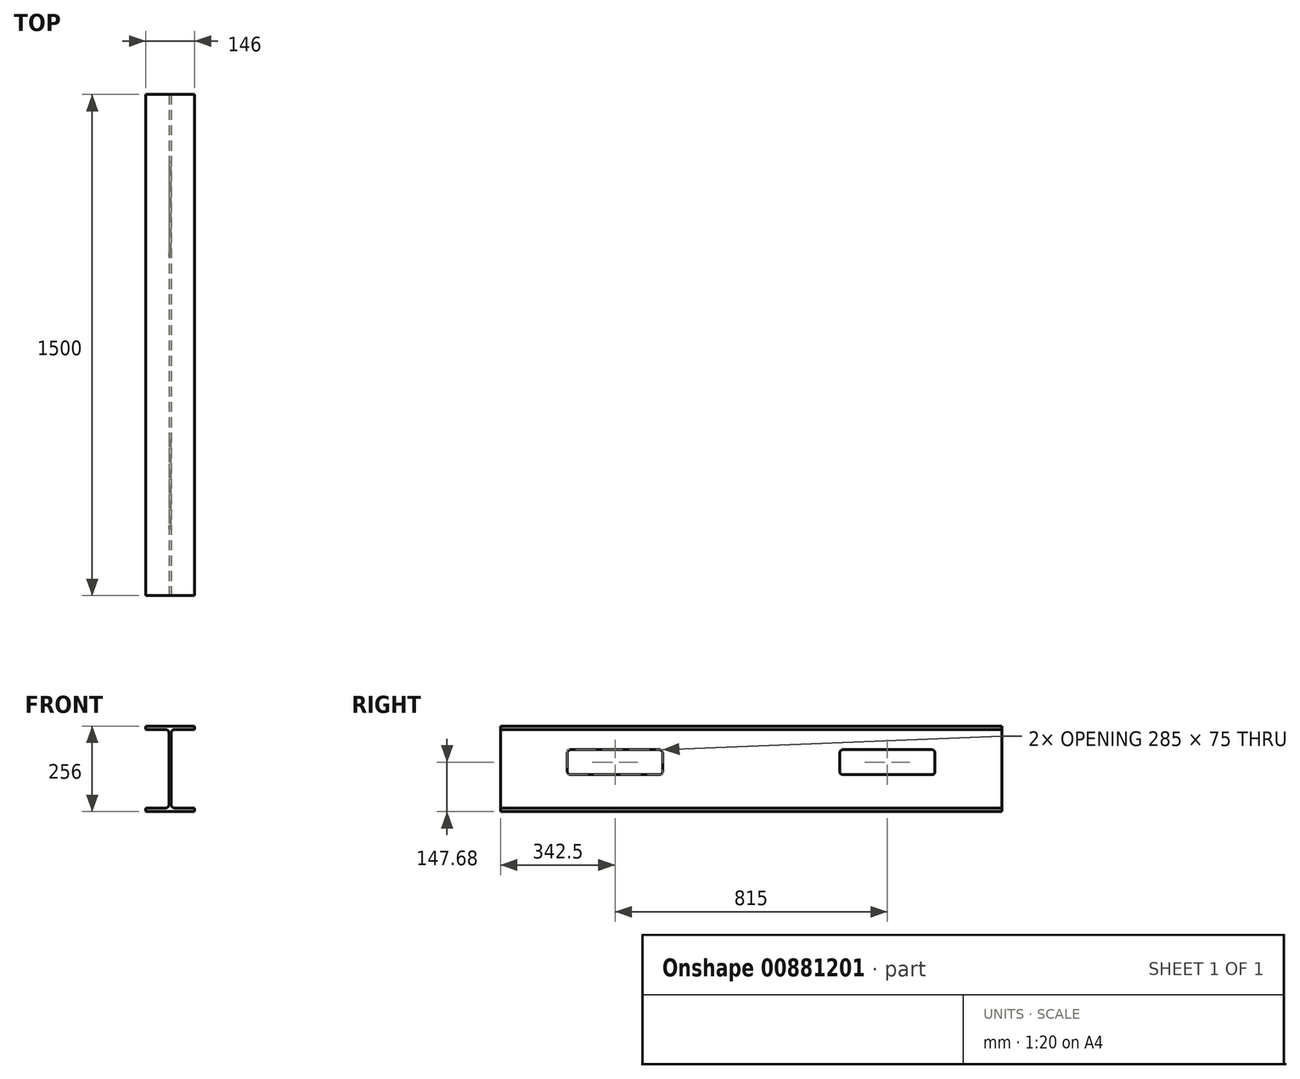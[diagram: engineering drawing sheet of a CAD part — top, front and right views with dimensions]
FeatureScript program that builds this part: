
annotation { "Feature Type Name" : "Feature", "Feature Type Description" : "" }
export const myFeature = defineFeature(function(context is Context, id is Id, definition is map)
    precondition{}
    {
        {
            var Q0;
            Q0=qCreatedBy(makeId("Front.planeOp"),FACE);
            var sketch = newSketch(context, id + "F0", { "sketchPlane" : qUnion([Q0])});
            skLineSegment(sketch, "E0", {"start": v(0, 147.9) * mm, "end": v(0, -157.79) * mm, "construction": true});
            skLineSegment(sketch, "E1", {"start": v(0, 108.32) * mm, "end": v(73, 108.32) * mm});
            skLineSegment(sketch, "E2", {"start": v(73, 108.32) * mm, "end": v(73, 97.42) * mm});
            skLineSegment(sketch, "E3", {"start": v(73, 97.42) * mm, "end": v(13.2, 97.42) * mm});
            skLineSegment(sketch, "E4", {"start": v(13.2, -136.78) * mm, "end": v(73, -136.78) * mm});
            skLineSegment(sketch, "E5", {"start": v(73, -136.78) * mm, "end": v(73, -147.68) * mm});
            skLineSegment(sketch, "E6", {"start": v(73, -147.68) * mm, "end": v(0, -147.68) * mm});
            skLineSegment(sketch, "E7", {"start": v(3.2, 87.42) * mm, "end": v(3.2, -126.78) * mm});
            skLineSegment(sketch, "E8.MirrorCS", {"start": v(0, 108.32) * mm, "end": v(-73, 108.32) * mm});
            skLineSegment(sketch, "E9.MirrorCS", {"start": v(-73, 108.32) * mm, "end": v(-73, 97.42) * mm});
            skLineSegment(sketch, "E10.MirrorCS", {"start": v(-73, 97.42) * mm, "end": v(-13.2, 97.42) * mm});
            skLineSegment(sketch, "E11.MirrorCS", {"start": v(-3.2, 87.42) * mm, "end": v(-3.2, -126.78) * mm});
            skLineSegment(sketch, "E12.MirrorCS", {"start": v(-13.2, -136.78) * mm, "end": v(-73, -136.78) * mm});
            skLineSegment(sketch, "E13.MirrorCS", {"start": v(-73, -136.78) * mm, "end": v(-73, -147.68) * mm});
            skLineSegment(sketch, "E14.MirrorCS", {"start": v(-73, -147.68) * mm, "end": v(0, -147.68) * mm});
            skPoint(sketch, "E15.visualSharp", {"position": v(3.2, 97.42) * mm});
            skArc(sketch, "E15.filletArc", {"start": v(13.2, 97.42) * mm, "mid": v(6.13, 94.5) * mm, "end": v(3.2, 87.42) * mm});
            skPoint(sketch, "E16.visualSharp", {"position": v(-3.2, 97.42) * mm});
            skArc(sketch, "E16.filletArc", {"start": v(-3.2, 87.42) * mm, "mid": v(-6.13, 94.5) * mm, "end": v(-13.2, 97.42) * mm});
            skPoint(sketch, "E17.visualSharp", {"position": v(-3.2, -136.78) * mm});
            skArc(sketch, "E17.filletArc", {"start": v(-13.2, -136.78) * mm, "mid": v(-6.13, -133.85) * mm, "end": v(-3.2, -126.78) * mm});
            skPoint(sketch, "E18.visualSharp", {"position": v(3.2, -136.78) * mm});
            skArc(sketch, "E18.filletArc", {"start": v(3.2, -126.78) * mm, "mid": v(6.13, -133.85) * mm, "end": v(13.2, -136.78) * mm});
            skSolve(sketch);
        }
        {
            var Q0;
            Q0=makeQuery(id+"F0.imprint","IMPRINT",FACE,{"disambiguationData":[TD([[makeQuery(id+"F0.imprint","IMPRINT",EDGE,{"derivedFrom":sQuery(id+"F0.wireOp",EDGE,"E1")}),-1.0]])]});
            extrude(context, id + "F1", {"entities" : qUnion([Q0]), "oppositeDirection" : true, "depth" : 1500 * mm, "offsetDistance" : 25 * mm});
        }
        {
            var Q0;
            Q0=makeQuery(id+"F1.opExtrude","SWEPT_FACE",FACE,{"disambiguationData":[OSD([sQuery(id+"F0.wireOp",EDGE,"E7")])]});
            var sketch = newSketch(context, id + "F2", { "sketchPlane" : qUnion([Q0])});
            skLineSegment(sketch, "E19.bottom", {"start": v(210, 37.5) * mm, "end": v(475, 37.5) * mm});
            skLineSegment(sketch, "E19.top", {"start": v(210, -37.5) * mm, "end": v(475, -37.5) * mm});
            skLineSegment(sketch, "E19.left", {"start": v(200, 27.5) * mm, "end": v(200, -27.5) * mm});
            skLineSegment(sketch, "E19.right", {"start": v(485, 27.5) * mm, "end": v(485, -27.5) * mm});
            skLineSegment(sketch, "E20", {"start": v(0, 0) * mm, "end": v(1500, 0) * mm, "construction": true});
            skPoint(sketch, "E21.visualSharp", {"position": v(200, 37.5) * mm});
            skArc(sketch, "E21.filletArc", {"start": v(210, 37.5) * mm, "mid": v(202.93, 34.57) * mm, "end": v(200, 27.5) * mm});
            skPoint(sketch, "E22.visualSharp", {"position": v(485, 37.5) * mm});
            skArc(sketch, "E22.filletArc", {"start": v(485, 27.5) * mm, "mid": v(482.07, 34.57) * mm, "end": v(475, 37.5) * mm});
            skPoint(sketch, "E23.visualSharp", {"position": v(485, -37.5) * mm});
            skArc(sketch, "E23.filletArc", {"start": v(475, -37.5) * mm, "mid": v(482.07, -34.57) * mm, "end": v(485, -27.5) * mm});
            skPoint(sketch, "E24.visualSharp", {"position": v(200, -37.5) * mm});
            skArc(sketch, "E24.filletArc", {"start": v(200, -27.5) * mm, "mid": v(202.93, -34.57) * mm, "end": v(210, -37.5) * mm});
            skLineSegment(sketch, "E25.bottom", {"start": v(1025, 37.5) * mm, "end": v(1290, 37.5) * mm});
            skLineSegment(sketch, "E25.top", {"start": v(1025, -37.5) * mm, "end": v(1290, -37.5) * mm});
            skLineSegment(sketch, "E25.left", {"start": v(1015, 27.5) * mm, "end": v(1015, -27.5) * mm});
            skLineSegment(sketch, "E25.right", {"start": v(1300, 27.5) * mm, "end": v(1300, -27.5) * mm});
            skPoint(sketch, "E26.visualSharp", {"position": v(1015, 37.5) * mm});
            skArc(sketch, "E26.filletArc", {"start": v(1025, 37.5) * mm, "mid": v(1017.93, 34.57) * mm, "end": v(1015, 27.5) * mm});
            skPoint(sketch, "E27.visualSharp", {"position": v(1300, 37.5) * mm});
            skArc(sketch, "E27.filletArc", {"start": v(1300, 27.5) * mm, "mid": v(1297.07, 34.57) * mm, "end": v(1290, 37.5) * mm});
            skPoint(sketch, "E28.visualSharp", {"position": v(1300, -37.5) * mm});
            skArc(sketch, "E28.filletArc", {"start": v(1290, -37.5) * mm, "mid": v(1297.07, -34.57) * mm, "end": v(1300, -27.5) * mm});
            skPoint(sketch, "E29.visualSharp", {"position": v(1015, -37.5) * mm});
            skArc(sketch, "E29.filletArc", {"start": v(1015, -27.5) * mm, "mid": v(1017.93, -34.57) * mm, "end": v(1025, -37.5) * mm});
            skSolve(sketch);
        }
        {
            var Q0;
            Q0=makeQuery(id+"F2.imprint","IMPRINT",FACE,{"disambiguationData":[TD([[makeQuery(id+"F2.imprint","IMPRINT",EDGE,{"derivedFrom":sQuery(id+"F2.wireOp",EDGE,"E19.bottom")}),-1.0]])]});
            var Q1;
            Q1=makeQuery(id+"F2.imprint","IMPRINT",FACE,{"disambiguationData":[TD([[makeQuery(id+"F2.imprint","IMPRINT",EDGE,{"derivedFrom":sQuery(id+"F2.wireOp",EDGE,"E25.bottom")}),-1.0]])]});
            extrude(context, id + "F3", {"entities" : qUnion([Q0, Q1]), "operationType" : NewBodyOperationType.REMOVE, "endBound" : BoundingType.THROUGH_ALL, "oppositeDirection" : true, "depth" : 25 * mm, "offsetDistance" : 25 * mm});
        }
    });
